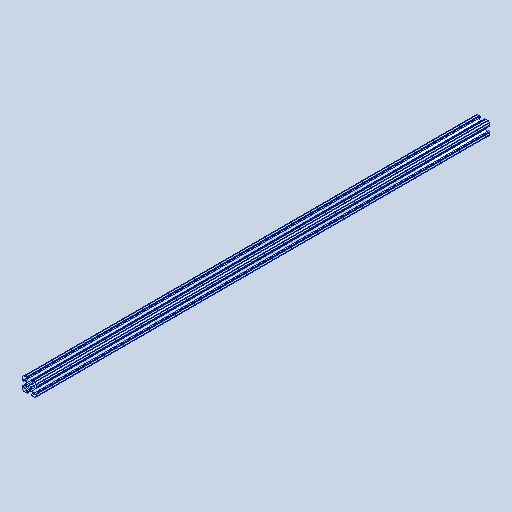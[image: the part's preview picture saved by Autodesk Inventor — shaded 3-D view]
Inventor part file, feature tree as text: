
AUTODESK INVENTOR PART (.ipt)
format: ipt  version: 2023 (Build 270158000, 158)  size: 326,144 bytes
history: native  units: in
note: dims shown in document units (in); Inventor stores cm internally (conversion verified against a paired STEP export)
features: extrude x1, sketch x1, projected_geometry x1, other x1
ambient origin geometry x8: Origin, YZ Plane, XZ Plane, XY Plane, X Axis, Y Axis, Z Axis, Center Point
bodies: Solid1 (feature_tree)
feature tree (4):
  extrude  "Extrusion1"  [1 undecoded]
  sketch  "Sketch1"  dims[d0=22.0in d1=0.0in]
  projected_geometry  "Projected Loop1"
  other  "Boss-Extrude1"
note: 1 required parameter value undecoded (feature->parameter linkage not recoverable at this tier; creation-order binding heuristic only, values carry confidence <= 0.55)
